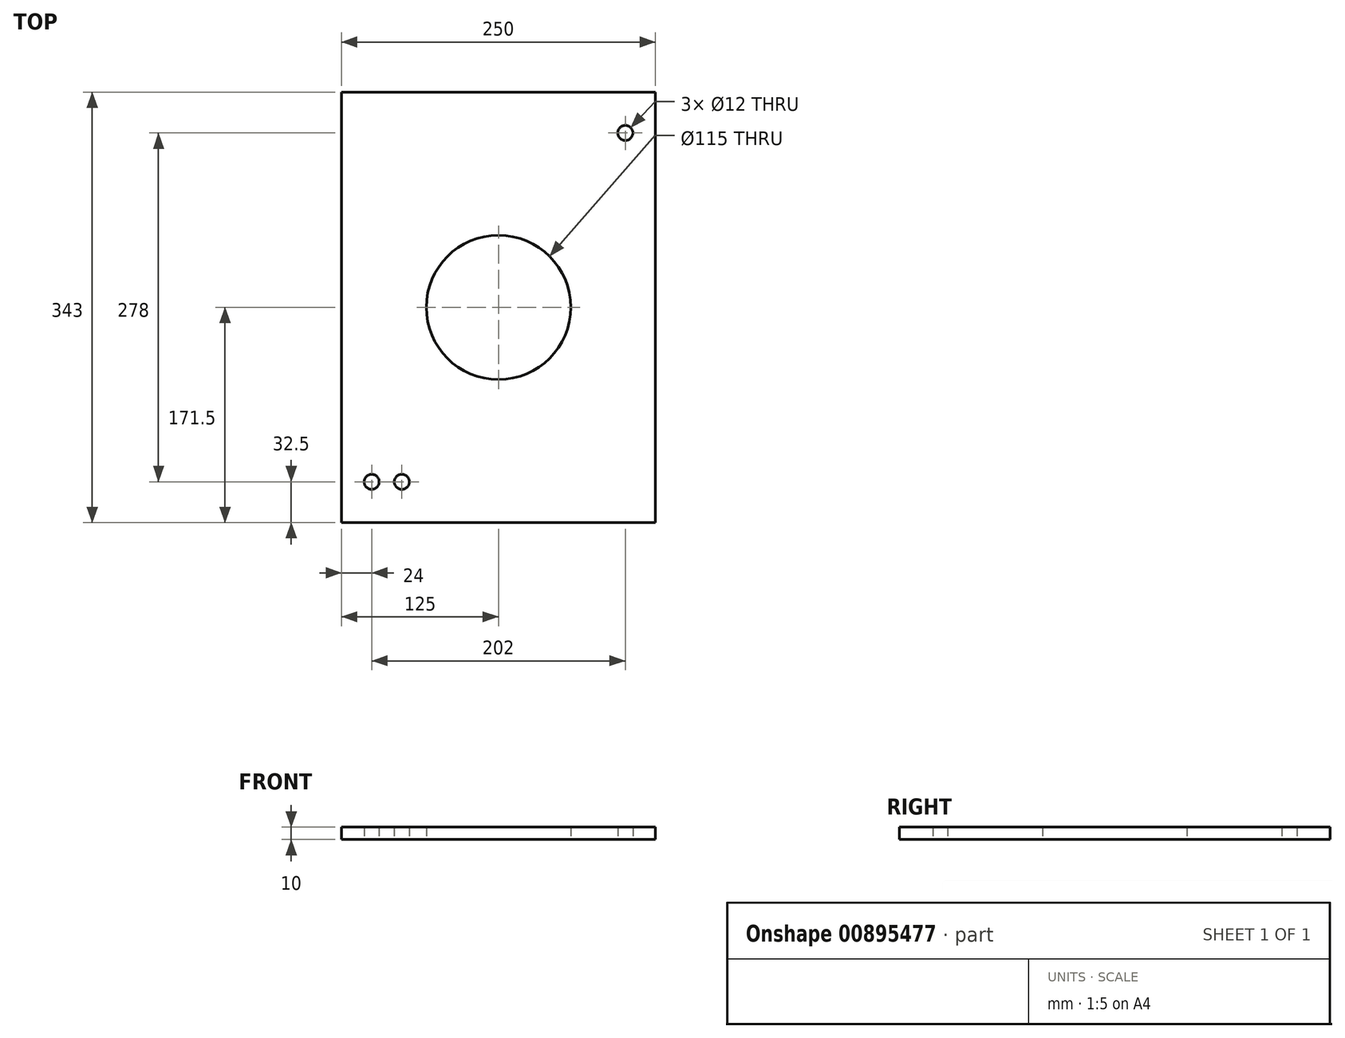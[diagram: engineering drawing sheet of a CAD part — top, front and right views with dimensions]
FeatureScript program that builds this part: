
annotation { "Feature Type Name" : "Feature", "Feature Type Description" : "" }
export const myFeature = defineFeature(function(context is Context, id is Id, definition is map)
    precondition{}
    {
        {
            var Q0;
            Q0=qCreatedBy(makeId("Top.planeOp"),FACE);
            var sketch = newSketch(context, id + "F0", { "sketchPlane" : qUnion([Q0])});
            skLineSegment(sketch, "E0.bottom", {"start": v(0, 0) * mm, "end": v(250, 0) * mm});
            skLineSegment(sketch, "E0.top", {"start": v(0, 343) * mm, "end": v(250, 343) * mm});
            skLineSegment(sketch, "E0.left", {"start": v(0, 0) * mm, "end": v(0, 343) * mm});
            skLineSegment(sketch, "E0.right", {"start": v(250, 0) * mm, "end": v(250, 343) * mm});
            skCircle(sketch, "E1", {"center": v(226, 310.5) * mm, "radius": 6 * mm});
            skCircle(sketch, "E2", {"center": v(24, 32.5) * mm, "radius": 6 * mm});
            skCircle(sketch, "E3", {"center": v(48, 32.5) * mm, "radius": 6 * mm});
            skCircle(sketch, "E4", {"center": v(125, 171.5) * mm, "radius": 57.5 * mm});
            skPoint(sketch, "E5", {"position": v(0, 171.5) * mm});
            skPoint(sketch, "E6", {"position": v(125, 343) * mm});
            skSolve(sketch);
        }
        {
            var Q0;
            Q0 = qSketchRegion(id + "F0", true);
            extrude(context, id + "F1", {"entities" : qUnion([Q0]), "depth" : 10 * mm, "offsetDistance" : 25 * mm});
        }
    });
